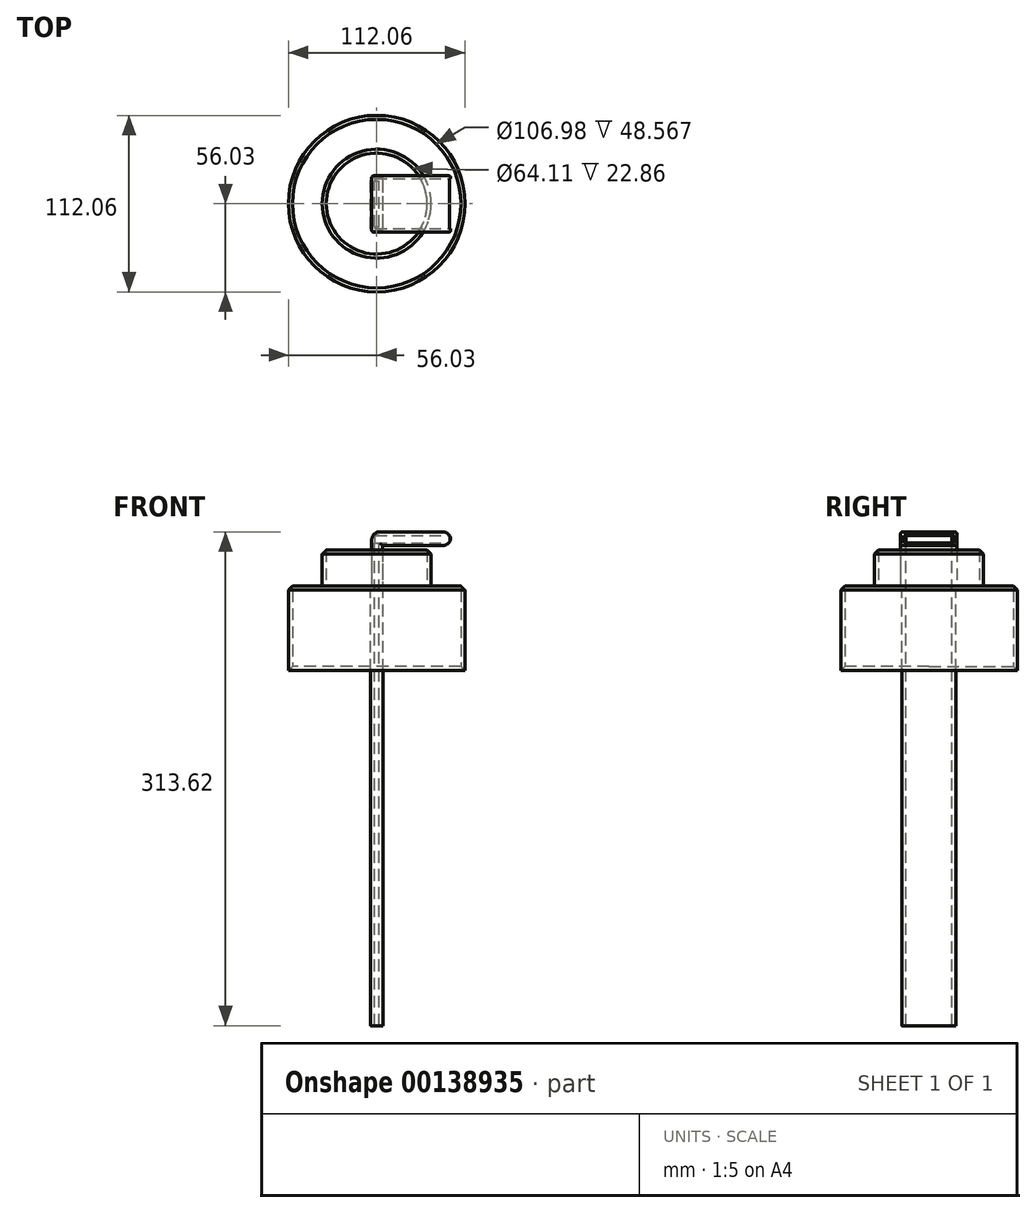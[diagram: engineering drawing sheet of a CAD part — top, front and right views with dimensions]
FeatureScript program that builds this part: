
annotation { "Feature Type Name" : "Feature", "Feature Type Description" : "" }
export const myFeature = defineFeature(function(context is Context, id is Id, definition is map)
    precondition{}
    {
        {
            var Q0;
            Q0=qCreatedBy(makeId("Top.planeOp"),FACE);
            var sketch = newSketch(context, id + "F0", { "sketchPlane" : qUnion([Q0])});
            skCircle(sketch, "E0", {"center": v(0, 0) * mm, "radius": 56.03 * mm});
            skSolve(sketch);
        }
        {
            var Q0;
            Q0 = qSketchRegion(id + "F0", true);
            extrude(context, id + "F1", {"entities" : qUnion([Q0]), "depth" : 56.19 * mm});
        }
        {
            var Q0;
            Q0=makeQuery(id+"F1.opExtrude","CAP_FACE",FACE,{"disambiguationData":[OSD([sQuery(id+"F0.wireOp",EDGE,"E0")])],"isStart":true});
            shell(context, id + "F2", {"entities" : qUnion([Q0]), "thickness" : 2.54 * mm});
        }
        {
            var Q0;
            {var subQ0=sQuery(id+"F0.wireOp",EDGE,"E0");Q0=makeQuery(id+"F2.opShell","OFFSET_FACE",FACE,{"disambiguationData":[OSD([subQ0]),TDD([makeQuery(id+"F1.opExtrude","CAP_FACE",FACE,{"disambiguationData":[OSD([subQ0])],"isStart":false})])]});}
            var sketch = newSketch(context, id + "F3", { "sketchPlane" : qUnion([Q0])});
            skLineSegment(sketch, "E1.bottom", {"start": v(-3.85, 17.27) * mm, "end": v(3.93, 17.27) * mm});
            skLineSegment(sketch, "E1.top", {"start": v(-3.85, -16.9) * mm, "end": v(3.93, -16.9) * mm});
            skLineSegment(sketch, "E1.left", {"start": v(-3.85, 17.27) * mm, "end": v(-3.85, -16.9) * mm});
            skLineSegment(sketch, "E1.right", {"start": v(3.93, 17.27) * mm, "end": v(3.93, -16.9) * mm});
            skSolve(sketch);
        }
        {
            var Q0;
            Q0 = qSketchRegion(id + "F3", true);
            extrude(context, id + "F4", {"entities" : qUnion([Q0]), "operationType" : NewBodyOperationType.ADD, "depth" : 276.6 * mm});
        }
        {
            var Q0;
            {var subQ0=sQuery(id+"F0.wireOp",EDGE,"E0");Q0=makeQuery(id+"F2.opShell","OFFSET_EDGE",EDGE,{"disambiguationData":[OSD([subQ0]),TDD([makeQuery(id+"F1.opExtrude","CAP_EDGE",EDGE,{"disambiguationData":[OSD([subQ0])],"isStart":true})])]});}
            chamfer(context, id + "F5", {"entities" : qUnion([Q0]), "width" : 5.08 * mm, "tangentPropagation" : true});
        }
        {
            var Q0;
            Q0=makeQuery(id+"F1.opExtrude","CAP_FACE",FACE,{"disambiguationData":[OSD([sQuery(id+"F0.wireOp",EDGE,"E0")])],"isStart":false});
            var sketch = newSketch(context, id + "F6", { "sketchPlane" : qUnion([Q0])});
            skCircle(sketch, "E2", {"center": v(0, 0) * mm, "radius": 34.6 * mm});
            skSolve(sketch);
        }
        {
            var Q0;
            Q0 = qSketchRegion(id + "F6", true);
            extrude(context, id + "F7", {"entities" : qUnion([Q0]), "operationType" : NewBodyOperationType.ADD, "depth" : 25.4 * mm});
        }
        {
            var Q0;
            Q0=makeQuery(id+"F7.opExtrude","CAP_FACE",FACE,{"disambiguationData":[OSD([sQuery(id+"F6.wireOp",EDGE,"E2")])],"isStart":false});
            var Q1;
            Q1=makeQuery(id+"F4.opExtrude","CAP_FACE",FACE,{"disambiguationData":[OSD([sQuery(id+"F3.wireOp",EDGE,"E1.bottom"),sQuery(id+"F3.wireOp",EDGE,"E1.top"),sQuery(id+"F3.wireOp",EDGE,"E1.left"),sQuery(id+"F3.wireOp",EDGE,"E1.right")])],"isStart":false});
            shell(context, id + "F8", {"entities" : qUnion([Q0, Q1]), "thickness" : 2.54 * mm});
        }
        {
            var Q0;
            Q0=makeQuery(id+"F7.opExtrude","CAP_EDGE",EDGE,{"disambiguationData":[OSD([sQuery(id+"F6.wireOp",EDGE,"E2")])],"isStart":false});
            var Q1;
            Q1=makeQuery(id+"F7.opExtrude","CAP_EDGE",EDGE,{"disambiguationData":[OSD([sQuery(id+"F6.wireOp",EDGE,"E2")])],"isStart":true});
            chamfer(context, id + "F9", {"entities" : qUnion([Q0, Q1]), "width" : 5.08 * mm, "tangentPropagation" : true});
        }
        {
            var Q0;
            Q0=makeQuery(id+"F1.opExtrude","CAP_EDGE",EDGE,{"disambiguationData":[OSD([sQuery(id+"F0.wireOp",EDGE,"E0")])],"isStart":false});
            chamfer(context, id + "F10", {"entities" : qUnion([Q0]), "width" : 2.54 * mm, "tangentPropagation" : true});
        }
        {
            var Q0;
            Q0=makeQuery(id+"F8.opShell","OFFSET_FACE",FACE,{"disambiguationData":[OSD([sQuery(id+"F0.wireOp",EDGE,"E0")])]});
            var sketch = newSketch(context, id + "F11", { "sketchPlane" : qUnion([Q0])});
            skLineSegment(sketch, "E3.bottom", {"start": v(-3.2, 17.64) * mm, "end": v(3.56, 17.64) * mm});
            skLineSegment(sketch, "E3.top", {"start": v(-3.2, -18.13) * mm, "end": v(3.56, -18.13) * mm});
            skLineSegment(sketch, "E3.left", {"start": v(-3.2, 17.64) * mm, "end": v(-3.2, -18.13) * mm});
            skLineSegment(sketch, "E3.right", {"start": v(3.56, 17.64) * mm, "end": v(3.56, -18.13) * mm});
            skSolve(sketch);
        }
        {
            var Q0;
            Q0 = qSketchRegion(id + "F11", true);
            extrude(context, id + "F12", {"entities" : qUnion([Q0]), "operationType" : NewBodyOperationType.ADD, "depth" : 28.28 * mm});
        }
        {
            var Q0;
            Q0=makeQuery(id+"F12.opExtrude","CAP_FACE",FACE,{"disambiguationData":[OSD([sQuery(id+"F11.wireOp",EDGE,"E3.bottom"),sQuery(id+"F11.wireOp",EDGE,"E3.top"),sQuery(id+"F11.wireOp",EDGE,"E3.left"),sQuery(id+"F11.wireOp",EDGE,"E3.right")])],"isStart":false});
            var sketch = newSketch(context, id + "F13", { "sketchPlane" : qUnion([Q0])});
            skLineSegment(sketch, "E4.bottom", {"start": v(-3.2, 17.64) * mm, "end": v(3.56, 17.64) * mm});
            skLineSegment(sketch, "E4.top", {"start": v(-3.2, -18.13) * mm, "end": v(3.56, -18.13) * mm});
            skLineSegment(sketch, "E4.left", {"start": v(-3.2, 17.64) * mm, "end": v(-3.2, -18.13) * mm});
            skLineSegment(sketch, "E4.right", {"start": v(3.56, 17.64) * mm, "end": v(3.56, -18.13) * mm});
            skSolve(sketch);
        }
        {
            var Q0;
            Q0 = qSketchRegion(id + "F13", true);
            extrude(context, id + "F14", {"entities" : qUnion([Q0]), "operationType" : NewBodyOperationType.ADD, "depth" : 6.2 * mm});
        }
        {
            var Q0;
            Q0=makeQuery(id+"F14.boolean.opBoolean","MERGE",FACE,{"derivedFrom":[makeQuery(id+"F12.opExtrude","SWEPT_FACE",FACE,{"disambiguationData":[OSD([sQuery(id+"F11.wireOp",EDGE,"E3.right")])]}),makeQuery(id+"F14.opExtrude","SWEPT_FACE",FACE,{"disambiguationData":[OSD([sQuery(id+"F13.wireOp",EDGE,"E4.right")])]})]});
            var sketch = newSketch(context, id + "F15", { "sketchPlane" : qUnion([Q0])});
            skLineSegment(sketch, "E5.bottom", {"start": v(-18.13, 90.66) * mm, "end": v(17.64, 90.66) * mm});
            skLineSegment(sketch, "E5.top", {"start": v(-18.13, 82.06) * mm, "end": v(17.64, 82.06) * mm});
            skLineSegment(sketch, "E5.left", {"start": v(-18.13, 90.66) * mm, "end": v(-18.13, 82.06) * mm});
            skLineSegment(sketch, "E5.right", {"start": v(17.64, 90.66) * mm, "end": v(17.64, 82.06) * mm});
            skSolve(sketch);
        }
        {
            var Q0;
            Q0 = qSketchRegion(id + "F15", true);
            extrude(context, id + "F16", {"entities" : qUnion([Q0]), "operationType" : NewBodyOperationType.ADD, "depth" : 43.52 * mm});
        }
        {
            var Q0;
            Q0=makeQuery(id+"F16.opExtrude","CAP_FACE",FACE,{"disambiguationData":[OSD([sQuery(id+"F15.wireOp",EDGE,"E5.bottom"),sQuery(id+"F15.wireOp",EDGE,"E5.top"),sQuery(id+"F15.wireOp",EDGE,"E5.left"),sQuery(id+"F15.wireOp",EDGE,"E5.right")])],"isStart":false});
            var sketch = newSketch(context, id + "F17", { "sketchPlane" : qUnion([Q0])});
            skLineSegment(sketch, "E6.bottom", {"start": v(-15.89, 88.54) * mm, "end": v(15.96, 88.54) * mm});
            skLineSegment(sketch, "E6.top", {"start": v(-15.89, 83.73) * mm, "end": v(15.96, 83.73) * mm});
            skLineSegment(sketch, "E6.left", {"start": v(-15.89, 88.54) * mm, "end": v(-15.89, 83.73) * mm});
            skLineSegment(sketch, "E6.right", {"start": v(15.96, 88.54) * mm, "end": v(15.96, 83.73) * mm});
            skSolve(sketch);
        }
        {
            var Q0;
            Q0 = qSketchRegion(id + "F17", true);
            extrude(context, id + "F18", {"entities" : qUnion([Q0]), "operationType" : NewBodyOperationType.REMOVE, "oppositeDirection" : true, "depth" : 48.08 * mm});
        }
        {
            var Q0;
            Q0=makeQuery(id+"F12.opExtrude","CAP_FACE",FACE,{"disambiguationData":[OSD([sQuery(id+"F11.wireOp",EDGE,"E3.bottom"),sQuery(id+"F11.wireOp",EDGE,"E3.top"),sQuery(id+"F11.wireOp",EDGE,"E3.left"),sQuery(id+"F11.wireOp",EDGE,"E3.right")])],"isStart":true});
            extrude(context, id + "F19", {"entities" : qUnion([Q0]), "operationType" : NewBodyOperationType.REMOVE, "oppositeDirection" : true, "depth" : 32.4 * mm});
        }
        {
            var Q0;
            Q0=makeQuery(id+"F14.opExtrude","CAP_EDGE",EDGE,{"disambiguationData":[OSD([sQuery(id+"F13.wireOp",EDGE,"E4.left")])],"isStart":false});
            fillet(context, id + "F20", {"entities" : qUnion([Q0]), "radius" : 5.08 * mm, "tangentPropagation" : true, "allowEdgeOverflow" : false});
        }
        {
            var Q0;
            Q0=makeQuery(id+"F16.opExtrude","CAP_EDGE",EDGE,{"disambiguationData":[OSD([sQuery(id+"F15.wireOp",EDGE,"E5.bottom")])],"isStart":false});
            var Q1;
            Q1=makeQuery(id+"F16.opExtrude","CAP_EDGE",EDGE,{"disambiguationData":[OSD([sQuery(id+"F15.wireOp",EDGE,"E5.top")])],"isStart":false});
            fillet(context, id + "F21", {"entities" : qUnion([Q0, Q1]), "radius" : 5.08 * mm, "tangentPropagation" : true, "allowEdgeOverflow" : false});
        }
        {
            var Q0;
            Q0=makeQuery(id+"F16.boolean.opBoolean","MERGE",EDGE,{"derivedFrom":[makeQuery(id+"F14.opExtrude","CAP_EDGE",EDGE,{"disambiguationData":[OSD([sQuery(id+"F13.wireOp",EDGE,"E4.top")])],"isStart":false}),makeQuery(id+"F16.opExtrude","SWEPT_EDGE",EDGE,{"disambiguationData":[OSD([sQuery(id+"F15.wireOp",EDGE,"E5.bottom"),sQuery(id+"F15.wireOp",EDGE,"E5.left")])]})]});
            var Q1;
            Q1=makeQuery(id+"F16.boolean.opBoolean","MERGE",EDGE,{"derivedFrom":[makeQuery(id+"F14.opExtrude","CAP_EDGE",EDGE,{"disambiguationData":[OSD([sQuery(id+"F13.wireOp",EDGE,"E4.bottom")])],"isStart":false}),makeQuery(id+"F16.opExtrude","SWEPT_EDGE",EDGE,{"disambiguationData":[OSD([sQuery(id+"F15.wireOp",EDGE,"E5.bottom"),sQuery(id+"F15.wireOp",EDGE,"E5.right")])]})]});
            var Q2;
            Q2=makeQuery(id+"F16.opExtrude","SWEPT_EDGE",EDGE,{"disambiguationData":[OSD([sQuery(id+"F11.wireOp",EDGE,"E3.top"),sQuery(id+"F11.wireOp",EDGE,"E3.right"),sQuery(id+"F13.wireOp",EDGE,"E4.top"),sQuery(id+"F13.wireOp",EDGE,"E4.right"),sQuery(id+"F15.wireOp",EDGE,"E5.top"),sQuery(id+"F15.wireOp",EDGE,"E5.left")])]});
            var Q3;
            Q3=makeQuery(id+"F16.opExtrude","SWEPT_EDGE",EDGE,{"disambiguationData":[OSD([sQuery(id+"F11.wireOp",EDGE,"E3.bottom"),sQuery(id+"F11.wireOp",EDGE,"E3.right"),sQuery(id+"F13.wireOp",EDGE,"E4.bottom"),sQuery(id+"F13.wireOp",EDGE,"E4.right"),sQuery(id+"F15.wireOp",EDGE,"E5.top"),sQuery(id+"F15.wireOp",EDGE,"E5.right")])]});
            var Q4;
            Q4=makeQuery(id+"F14.boolean.opBoolean","MERGE",EDGE,{"derivedFrom":[makeQuery(id+"F12.opExtrude","SWEPT_EDGE",EDGE,{"disambiguationData":[OSD([sQuery(id+"F11.wireOp",EDGE,"E3.top"),sQuery(id+"F11.wireOp",EDGE,"E3.right")])]}),makeQuery(id+"F14.opExtrude","SWEPT_EDGE",EDGE,{"disambiguationData":[OSD([sQuery(id+"F13.wireOp",EDGE,"E4.top"),sQuery(id+"F13.wireOp",EDGE,"E4.right")])]})]});
            var Q5;
            Q5=makeQuery(id+"F14.boolean.opBoolean","MERGE",EDGE,{"derivedFrom":[makeQuery(id+"F12.opExtrude","SWEPT_EDGE",EDGE,{"disambiguationData":[OSD([sQuery(id+"F11.wireOp",EDGE,"E3.bottom"),sQuery(id+"F11.wireOp",EDGE,"E3.right")])]}),makeQuery(id+"F14.opExtrude","SWEPT_EDGE",EDGE,{"disambiguationData":[OSD([sQuery(id+"F13.wireOp",EDGE,"E4.bottom"),sQuery(id+"F13.wireOp",EDGE,"E4.right")])]})]});
            var Q6;
            Q6=makeQuery(id+"F4.opExtrude","SWEPT_EDGE",EDGE,{"disambiguationData":[OSD([sQuery(id+"F3.wireOp",EDGE,"E1.top"),sQuery(id+"F3.wireOp",EDGE,"E1.right")])]});
            var Q7;
            Q7=makeQuery(id+"F4.opExtrude","SWEPT_EDGE",EDGE,{"disambiguationData":[OSD([sQuery(id+"F3.wireOp",EDGE,"E1.bottom"),sQuery(id+"F3.wireOp",EDGE,"E1.right")])]});
            var Q8;
            Q8=makeQuery(id+"F4.opExtrude","SWEPT_EDGE",EDGE,{"disambiguationData":[OSD([sQuery(id+"F3.wireOp",EDGE,"E1.top"),sQuery(id+"F3.wireOp",EDGE,"E1.left")])]});
            var Q9;
            Q9=makeQuery(id+"F4.opExtrude","SWEPT_EDGE",EDGE,{"disambiguationData":[OSD([sQuery(id+"F3.wireOp",EDGE,"E1.bottom"),sQuery(id+"F3.wireOp",EDGE,"E1.left")])]});
            fillet(context, id + "F22", {"entities" : qUnion([Q0, Q1, Q2, Q3, Q4, Q5, Q6, Q7, Q8, Q9]), "radius" : 1.27 * mm, "tangentPropagation" : true, "allowEdgeOverflow" : false});
        }
    });
